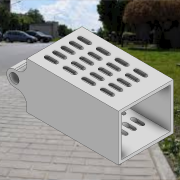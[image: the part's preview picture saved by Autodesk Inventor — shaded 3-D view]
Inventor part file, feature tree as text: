
AUTODESK INVENTOR PART (.ipt)
format: ipt  version: 2021 (Build 250183000, 183)  size: 452,096 bytes
history: native  units: mm
features: sketch x6, extrude x5, plane x2, pattern_linear x1, mirror x1, hole x1, fillet x1, projected_geometry x1
ambient origin geometry x8: Origin, YZ Plane, XZ Plane, XY Plane, X Axis, Y Axis, Z Axis, Center Point
bodies: Solid1 (feature_tree)
feature tree (18):
  sketch  "Sketch1"  dims[d0=45.0mm d1=53.0mm]
  extrude  "Extrusion1"  Depth=53.0mm
  extrude  "Extrusion2"  Depth=85.0mm TaperAngle=0.0deg
  sketch  "Sketch3"  dims[d2=3.0mm d11=85.0mm d12=0.0mm]
  plane  "Work Plane1"
  extrude  "Extrusion3"  Depth=3.0mm
  pattern_linear  "Rectangular Pattern1"  Spacing1=33.0mm  [1 undecoded]
  mirror  "Mirror1"
  plane  "Work Plane2"
  extrude  "Extrusion11"  Depth=50.0mm
  extrude  "Extrusion12"  [1 undecoded]
  hole  "Hole2"  [1 undecoded]
  fillet  "Fillet3"  Radius=3.0mm
  sketch  "Sketch5"  dims[d13=3.0mm d14=0.0mm d16=42.5mm]
  sketch  "Sketch12"  dims[d17=-7.853982mm]
  sketch  "Sketch13"  dims[d19=4.0mm]
  projected_geometry  "Projected Loop6"
  sketch  "Sketch14"  dims[d20=5.0mm d21=33.0mm d22=0.0mm d23=50.0mm d25=8.0mm d26=40.0mm d28=18.0mm d32=-6.5mm d48=3.0mm d49=3.0mm d50=3.0mm d79=3.0mm d80=3.0mm d81=86.0mm d82=0.0mm d83=7.0mm d84=0.0mm d85=15.0mm d86=12.0mm d87=15.0mm d88=0.0mm d89=9.0mm d90=6.0mm d91=15.0mm d92=9.0mm d93=90.0deg d94=8.0mm d95=20.594885mm d96=10.0mm d61=0.5mm d62=0.872665mm d63=0.5mm d64=0.872665mm]
note: 3 required parameter values undecoded (feature->parameter linkage not recoverable at this tier; creation-order binding heuristic only, values carry confidence <= 0.55)
